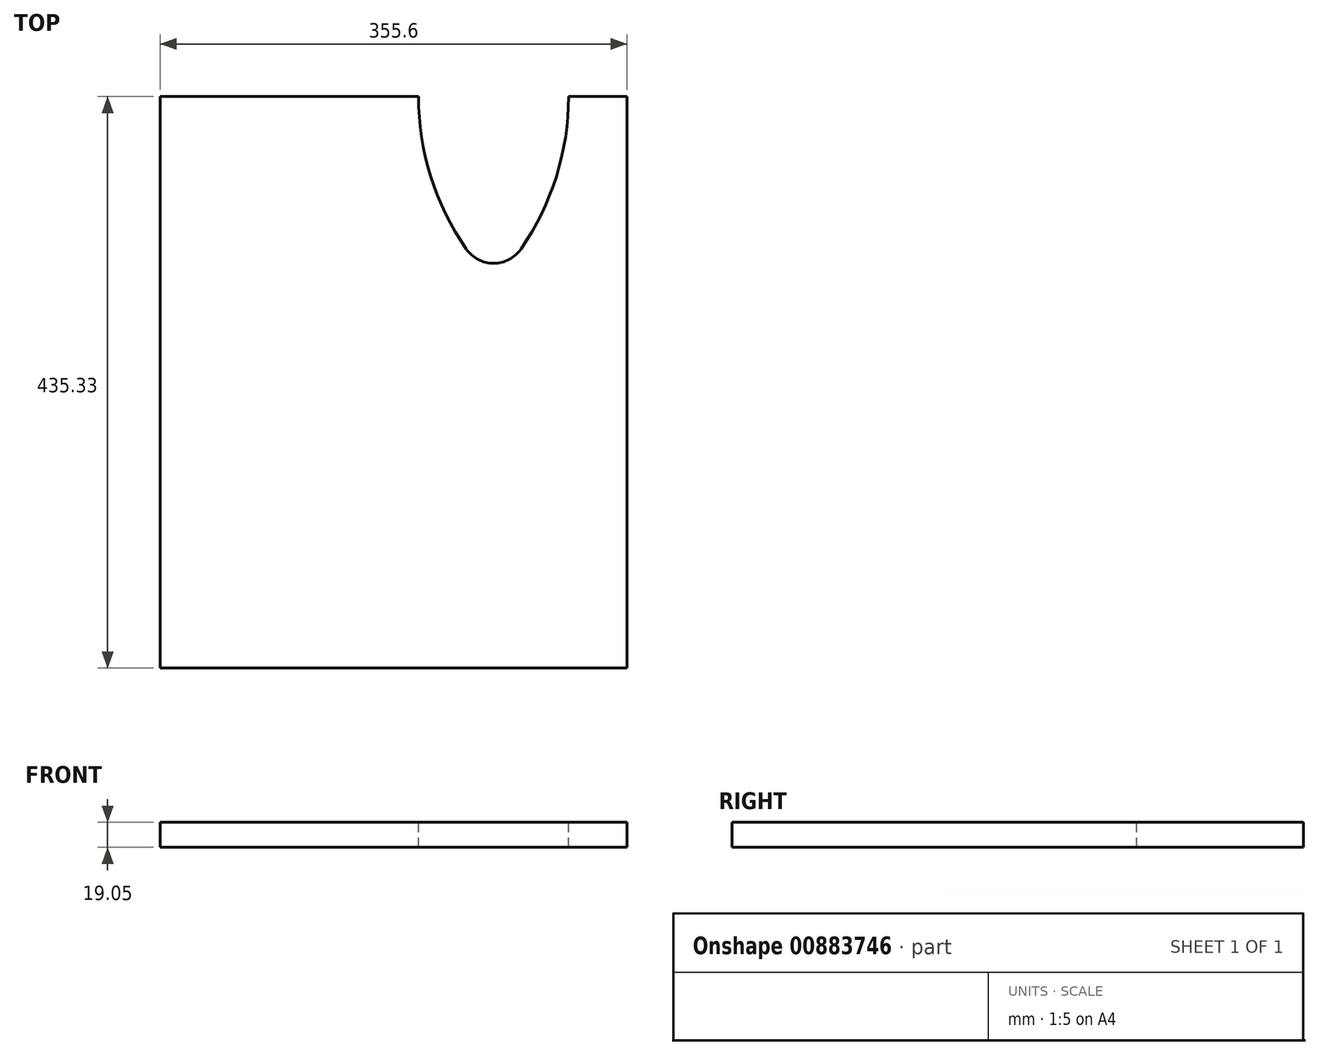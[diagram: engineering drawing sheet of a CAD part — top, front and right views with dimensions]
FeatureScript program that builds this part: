
annotation { "Feature Type Name" : "Feature", "Feature Type Description" : "" }
export const myFeature = defineFeature(function(context is Context, id is Id, definition is map)
    precondition{}
    {
        {
            var Q0;
            Q0=qCreatedBy(makeId("Top.planeOp"),FACE);
            var sketch = newSketch(context, id + "F0", { "sketchPlane" : qUnion([Q0])});
            skLineSegment(sketch, "E0", {"start": v(76.2, -127) * mm, "end": v(76.2, 121.9) * mm, "construction": true});
            skArc(sketch, "E1", {"start": v(55.32, -116.06) * mm, "mid": v(76.2, -127) * mm, "end": v(97.08, -116.06) * mm});
            skArc(sketch, "E2", {"start": v(133.35, 0) * mm, "mid": v(76.2, 57.15) * mm, "end": v(19.05, 0) * mm});
            skArc(sketch, "E3", {"start": v(19.05, 0) * mm, "mid": v(28.33, -60.8) * mm, "end": v(55.32, -116.06) * mm});
            skArc(sketch, "E4.MirrorC", {"start": v(133.35, 0) * mm, "mid": v(124.07, -60.8) * mm, "end": v(97.08, -116.06) * mm});
            skLineSegment(sketch, "E5", {"start": v(0, 0) * mm, "end": v(0, -189.46) * mm, "construction": true});
            skArc(sketch, "E6.MirrorCS", {"start": v(-55.32, -116.06) * mm, "mid": v(-76.2, -127) * mm, "end": v(-97.08, -116.06) * mm});
            skArc(sketch, "E7.MirrorCS", {"start": v(-19.05, 0) * mm, "mid": v(-28.33, -60.8) * mm, "end": v(-55.32, -116.06) * mm});
            skLineSegment(sketch, "E8.MirrorCS", {"start": v(-76.2, -127) * mm, "end": v(-76.2, 121.9) * mm, "construction": true});
            skArc(sketch, "E9.MirrorCS", {"start": v(-133.35, 0) * mm, "mid": v(-76.2, 57.15) * mm, "end": v(-19.05, 0) * mm});
            skArc(sketch, "E10.MirrorCS", {"start": v(-133.35, 0) * mm, "mid": v(-124.07, -60.8) * mm, "end": v(-97.08, -116.06) * mm});
            skSolve(sketch);
        }
        {
            var Q0;
            Q0=qCreatedBy(makeId("Top.planeOp"),FACE);
            var sketch = newSketch(context, id + "F1", { "sketchPlane" : qUnion([Q0])});
            skLineSegment(sketch, "E11.bottom", {"start": v(-177.8, 0) * mm, "end": v(177.8, 0) * mm});
            skLineSegment(sketch, "E11.top", {"start": v(-177.8, -435.33) * mm, "end": v(177.8, -435.33) * mm});
            skLineSegment(sketch, "E11.left", {"start": v(-177.8, 0) * mm, "end": v(-177.8, -435.33) * mm});
            skLineSegment(sketch, "E11.right", {"start": v(177.8, 0) * mm, "end": v(177.8, -435.33) * mm});
            skSolve(sketch);
        }
        {
            var Q0;
            Q0=makeQuery(id+"F1.imprint","IMPRINT",FACE,{"disambiguationData":[TD([[makeQuery(id+"F1.imprint","IMPRINT",EDGE,{"derivedFrom":sQuery(id+"F1.wireOp",EDGE,"E11.bottom")}),-1.0]])]});
            extrude(context, id + "F2", {"entities" : qUnion([Q0]), "oppositeDirection" : true, "depth" : 19.05 * mm, "offsetDistance" : 25.4 * mm});
        }
        {
            var Q0;
            Q0=makeQuery(id+"F0.imprint","IMPRINT",FACE,{"disambiguationData":[TD([[makeQuery(id+"F0.imprint","IMPRINT",EDGE,{"derivedFrom":sQuery(id+"F0.wireOp",EDGE,"E6.MirrorCS")}),-1.0]])]});
            var Q1;
            Q1=makeQuery(id+"F0.imprint","IMPRINT",FACE,{"disambiguationData":[TD([[makeQuery(id+"F0.imprint","IMPRINT",EDGE,{"derivedFrom":sQuery(id+"F0.wireOp",EDGE,"E1")}),1.0]])]});
            extrude(context, id + "F3", {"entities" : qUnion([Q0, Q1]), "operationType" : NewBodyOperationType.REMOVE, "endBound" : BoundingType.THROUGH_ALL, "oppositeDirection" : true, "depth" : 25.4 * mm, "offsetDistance" : 25.4 * mm});
        }
    });
